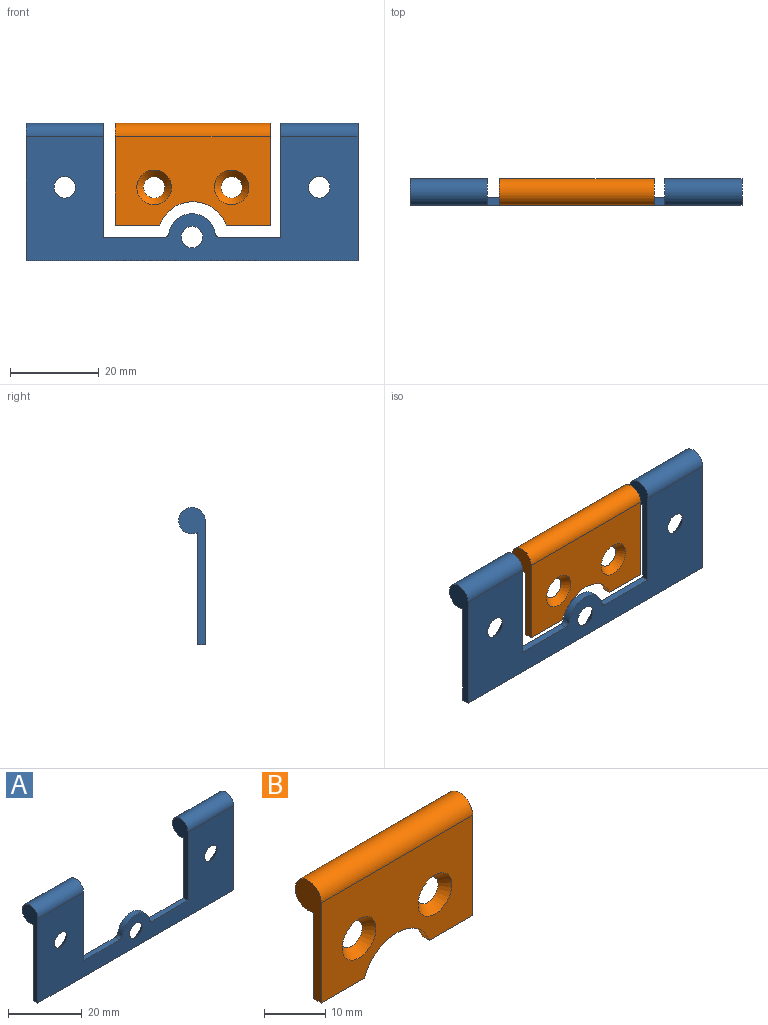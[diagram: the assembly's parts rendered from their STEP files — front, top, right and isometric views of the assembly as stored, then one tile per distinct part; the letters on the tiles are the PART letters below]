
ASSEMBLY  parts=2 mates=1
PART A: 17 faces, bbox 75x6x31 mm
  f0: plane 13.78x1.7mm, normal (0,0,1), area 23.4mm2, adj f2,f5,f9,f12
  f1: cylinder r=3mm len=17.5mm, axis (-1,0,0), area 270.9mm2, adj f2,f5,f7,f9
  f2: plane 75x28mm, normal (0,-1,0), area 1181mm2, adj f0,f1,f3,f4,f6,f7,f8,f9
  f3: cylinder r=3mm len=17.5mm, axis (-1,0,0), area 270.9mm2, adj f2,f5,f6,f8
  f4: plane 75x1.7mm, normal (0,0,-1), area 127.5mm2, adj f2,f5,f6,f7
  f5: plane 75x25.3mm, normal (0,1,0), area 998.3mm2, adj f0,f1,f3,f4,f6,f7,f8,f9
  f6: plane 31x6mm, normal (1,0,0), area 72.6mm2, adj f2,f3,f4,f5
  f7: plane 31x6mm, normal (-1,0,0), area 72.6mm2, adj f1,f2,f4,f5
  f8: plane 25.7x6mm, normal (-1,0,0), area 63.6mm2, adj f2,f3,f5,f10
  f9: plane 25.7x6mm, normal (1,0,0), area 63.6mm2, adj f0,f1,f2,f5
  f10: plane 13.78x1.7mm, normal (0,0,1), area 23.4mm2, adj f2,f5,f8,f13
  f11: cylinder r=5.3mm len=10.46mm, axis (0,-1,0), area 25.4mm2, adj f2,f5,f12,f13
  f12: cylinder r=1mm len=1.7mm, axis (0,-1,0), area 2.4mm2, adj f0,f2,f5,f11
  f13: cylinder r=1mm len=1.7mm, axis (0,-1,0), area 2.4mm2, adj f2,f5,f10,f11
  f14: cone r=1.9mm half-angle=41deg, axis (0,1,0), area 44.7mm2, adj f2,f5
  f15: cone r=1.9mm half-angle=41deg, axis (0,1,0), area 44.7mm2, adj f2,f5
  f16: cone r=1.9mm half-angle=41deg, axis (0,1,0), area 44.7mm2, adj f2,f5
PART B: 10 faces, bbox 35x6x23 mm
  f0: plane 9.97x1.7mm, normal (0,0,-1), area 17mm2, adj f1,f3,f5,f7
  f1: plane 35x17.3mm, normal (0,1,0), area 510.5mm2, adj f0,f2,f4,f5,f6,f7,f8,f9
  f2: cylinder r=3mm len=35mm, axis (-1,0,0), area 541.9mm2, adj f1,f3,f5,f6
  f3: plane 35x20mm, normal (0,-1,0), area 546.4mm2, adj f0,f2,f4,f5,f6,f7,f8,f9
  f4: plane 9.97x1.7mm, normal (0,0,-1), area 17mm2, adj f1,f3,f6,f7
  f5: plane 23x6mm, normal (1,0,0), area 59mm2, adj f0,f1,f2,f3
  f6: plane 23x6mm, normal (-1,0,0), area 59mm2, adj f1,f2,f3,f4
  f7: cylinder r=8mm len=15.05mm, axis (0,1,0), area 33.3mm2, adj f0,f1,f3,f4
  f8: cone r=1.9mm half-angle=41deg, axis (0,-1,0), area 44.7mm2, adj f1,f3
  f9: cone r=1.9mm half-angle=41deg, axis (0,-1,0), area 44.7mm2, adj f1,f3
PLACE A t=(-16.26,-15.72,-1.84)mm
PLACE B t=(-16.06,-15.72,-1.84)mm
MATE revolute A.f1 <-> B.f2  axis (-1,0,0) through (-36.26,-15.72,-1.84)mm
